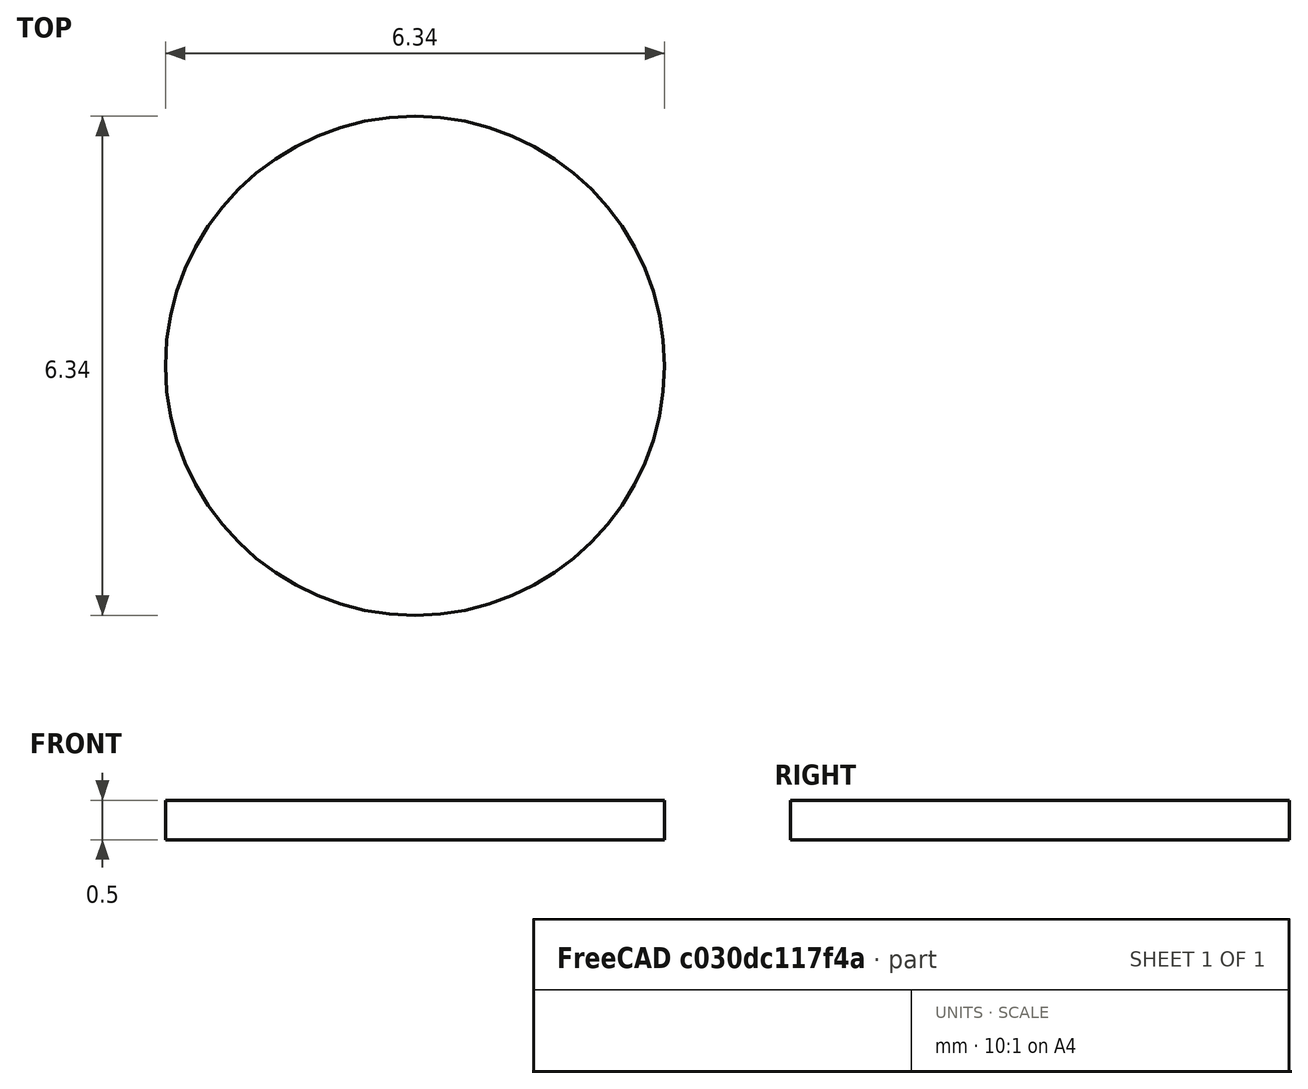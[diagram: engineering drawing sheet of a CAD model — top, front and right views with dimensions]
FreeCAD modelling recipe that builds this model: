
FCSTD DOCUMENT  (FreeCAD 1.1R14555 (Git shallow))
Label: 3M_SJ5382
License: All rights reserved
LicenseURL: https://en.wikipedia.org/wiki/All_rights_reserved
objects: App::Point×1, Sketcher::SketchObject×1, PartDesign::Revolution×1, PartDesign::Body×1
note: 6 computed .brp shape members not serialized (recipe doc carries the construction recipe); baked Part::Feature solids carry a one-line shape summary decoded from their .brp

FEATURE [App::Point] Origin001
  Role = Origin
FEATURE [Sketcher::SketchObject] Sketch
  ArcFitTolerance = 1e-06
  AttachmentSupport = -> [Origin]
  ExternalTypes = [0]
  FullyConstrained = true
  MakeInternals = false
  MapMode = 5
  Placement = pos=(0,0,0) rot=(1,0,0;1.5708rad)
  sketch-geometry (5):
    g0: LineSegment StartX=0 StartY=0 StartZ=0 EndX=6.50065e-11 EndY=1.9 EndZ=0
    g1: LineSegment StartX=0 StartY=0 StartZ=0 EndX=3.17 EndY=0 EndZ=0
    g2: LineSegment StartX=3.17 StartY=0 StartZ=0 EndX=3.17 EndY=0.5 EndZ=0
    g3: ArcOfCircle CenterX=-1.10968e-05 CenterY=-2.38892 CenterZ=0 NormalX=0 NormalY=0 NormalZ=1 AngleXU=0 Radius=4.28892 StartAngle=0.739038 EndAngle=1.57079
    g4: LineSegment [constr] StartX=6.50065e-11 StartY=1.9 StartZ=0 EndX=2 EndY=1.9 EndZ=0
  constraints (15):
    c: Coincident(g0,g-1)
    c: PointOnObject(g0,g-2)
    c: Coincident(g1,g0)
    c: PointOnObject(g1,g-1)
    c: DistanceY(g0,g0) = 1.9
    c: Coincident(g2,g1)
    c: Vertical(g2)
    c: Coincident(g3,g0)
    c: Coincident(g3,g2)
    c: DistanceX(g1,g1) = 3.17
    c: DistanceY(g2,g2) = 0.5
    c: Coincident(g4,g0)
    c: Horizontal(g4)
    c: Tangent(g4,g3)
    c: DistanceX(g4,g4) = 2
FEATURE [PartDesign::Revolution] Revolution
  Angle = 360
  Angle2 = 0
  Axis = (0,2e-16,1)
  Base = (0,0,0)
  Profile = -> Sketch
  ReferenceAxis = -> Sketch [V_Axis]
  Refine = true
  Reversed = true
  Suppressed = false
  Type = 0
FEATURE [PartDesign::Body] Body  label="3M_SJ5382"
  AllowCompound = true
  Group = -> [Sketch,Revolution]
  Origin = -> Origin
  Tip = -> Revolution
